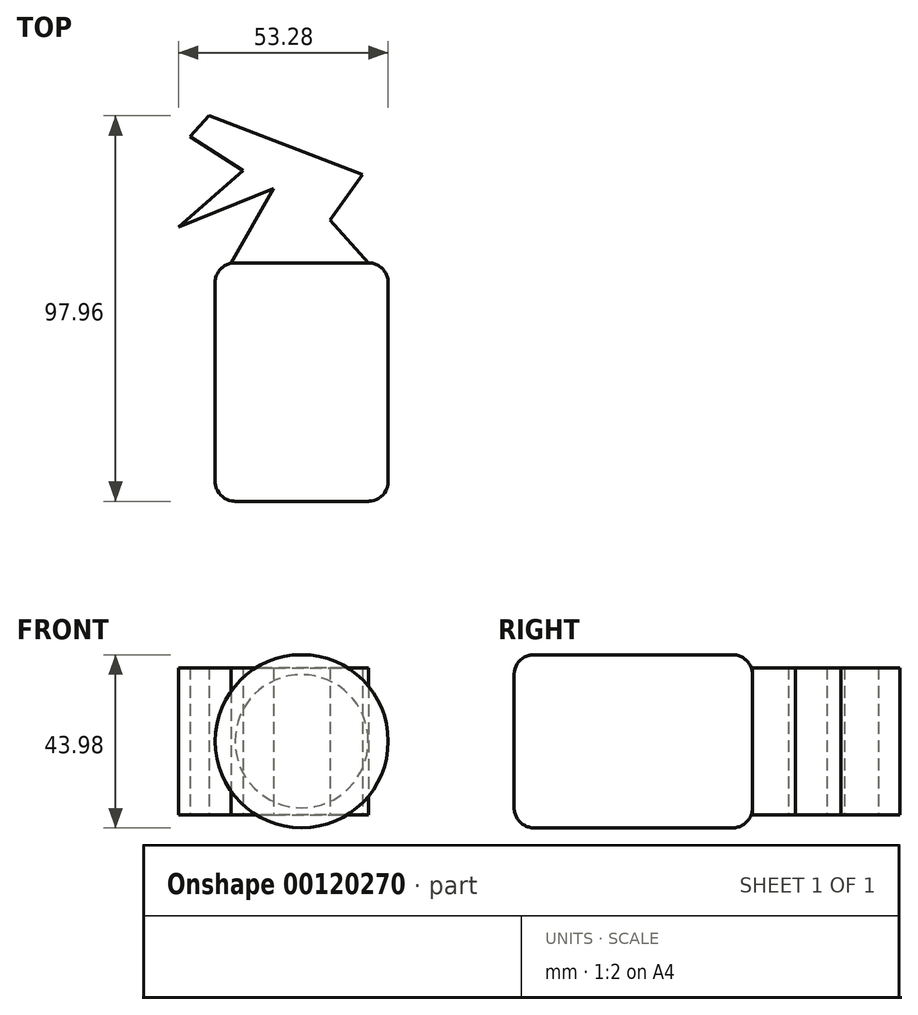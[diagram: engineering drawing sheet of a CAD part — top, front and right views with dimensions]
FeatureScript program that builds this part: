
annotation { "Feature Type Name" : "Feature", "Feature Type Description" : "" }
export const myFeature = defineFeature(function(context is Context, id is Id, definition is map)
    precondition{}
    {
        {
            var Q0;
            Q0=qCreatedBy(makeId("Front.planeOp"),FACE);
            var sketch = newSketch(context, id + "F0", { "sketchPlane" : qUnion([Q0])});
            skCircle(sketch, "E0", {"center": v(0, 0) * mm, "radius": 22 * mm});
            skSolve(sketch);
        }
        {
            var Q0;
            Q0=makeQuery(id+"F0.imprint","IMPRINT",FACE,{"disambiguationData":[TD([[makeQuery(id+"F0.imprint","IMPRINT",EDGE,{"derivedFrom":sQuery(id+"F0.wireOp",EDGE,"E0")}),1.0]])]});
            extrude(context, id + "F1", {"entities" : qUnion([Q0]), "depth" : 60.56 * mm});
        }
        {
            var Q0;
            Q0=makeQuery(id+"F1.opExtrude","SWEPT_FACE",FACE,{"disambiguationData":[OSD([sQuery(id+"F0.wireOp",EDGE,"E0")])]});
            fillet(context, id + "F2", {"entities" : qUnion([Q0]), "radius" : 5.08 * mm, "tangentPropagation" : true, "allowEdgeOverflow" : false});
        }
        {
            var Q0;
            Q0=qCreatedBy(makeId("Top.planeOp"),FACE);
            var sketch = newSketch(context, id + "F3", { "sketchPlane" : qUnion([Q0])});
            skLineSegment(sketch, "E1", {"start": v(17, 0) * mm, "end": v(7.15, 10.88) * mm});
            skLineSegment(sketch, "E2", {"start": v(7.15, 10.88) * mm, "end": v(15.5, 22.5) * mm});
            skLineSegment(sketch, "E3", {"start": v(15.5, 22.5) * mm, "end": v(-23.54, 37.4) * mm});
            skLineSegment(sketch, "E4", {"start": v(-23.54, 37.4) * mm, "end": v(-28.3, 32.03) * mm});
            skLineSegment(sketch, "E5", {"start": v(-28.3, 32.03) * mm, "end": v(-14.9, 23.4) * mm});
            skLineSegment(sketch, "E6", {"start": v(-14.9, 23.4) * mm, "end": v(-31.29, 9.09) * mm});
            skLineSegment(sketch, "E7", {"start": v(-31.29, 9.09) * mm, "end": v(-7.15, 18.92) * mm});
            skLineSegment(sketch, "E8", {"start": v(-7.15, 18.92) * mm, "end": v(-17.88, 0) * mm});
            skLineSegment(sketch, "E9", {"start": v(-17.88, 0) * mm, "end": v(17, 0) * mm});
            skSolve(sketch);
        }
        {
            var Q0;
            Q0=makeQuery(id+"F3.imprint","IMPRINT",FACE,{"disambiguationData":[TD([[makeQuery(id+"F3.imprint","IMPRINT",EDGE,{"derivedFrom":sQuery(id+"F3.wireOp",EDGE,"E1")}),1.0]])]});
            extrude(context, id + "F4", {"entities" : qUnion([Q0]), "operationType" : NewBodyOperationType.ADD, "endBound" : BoundingType.SYMMETRIC, "depth" : 37.32 * mm});
        }
    });
